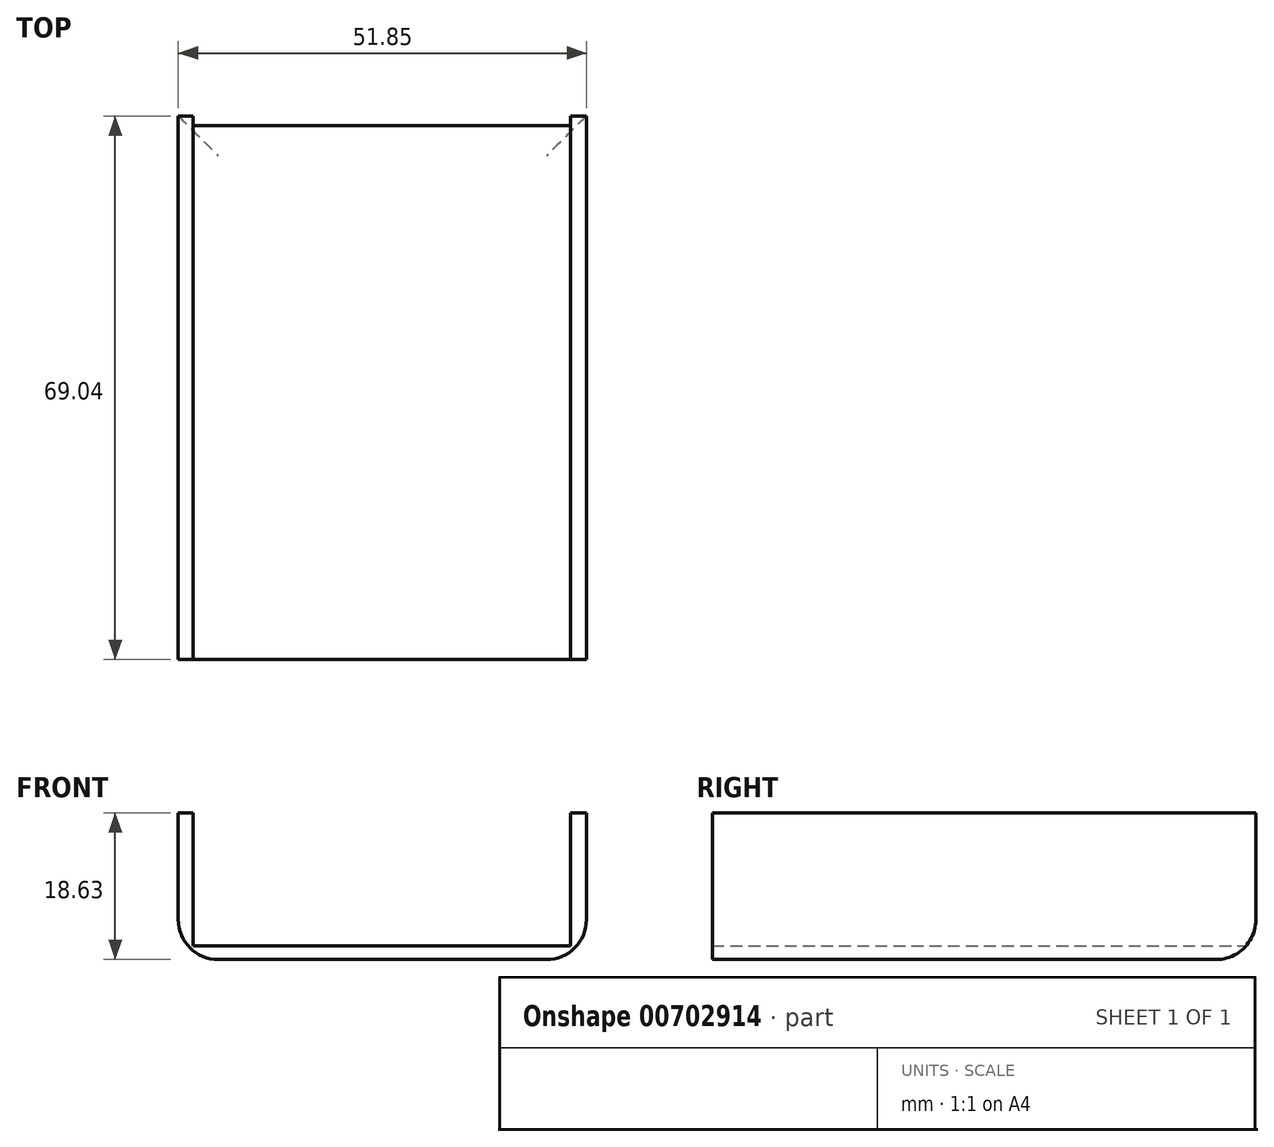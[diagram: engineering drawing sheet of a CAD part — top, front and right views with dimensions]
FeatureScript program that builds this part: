
annotation { "Feature Type Name" : "Feature", "Feature Type Description" : "" }
export const myFeature = defineFeature(function(context is Context, id is Id, definition is map)
    precondition{}
    {
        {
            var Q0;
            Q0=qCreatedBy(makeId("Front.planeOp"),FACE);
            var sketch = newSketch(context, id + "F0", { "sketchPlane" : qUnion([Q0])});
            skLineSegment(sketch, "E0.bottom", {"start": v(-24.96, -18.63) * mm, "end": v(26.89, -18.63) * mm});
            skLineSegment(sketch, "E0.left", {"start": v(-24.96, -18.63) * mm, "end": v(-24.96, 0) * mm});
            skLineSegment(sketch, "E0.right", {"start": v(26.89, -18.63) * mm, "end": v(26.89, 0) * mm});
            skPoint(sketch, "E0.middle", {"position": v(0, 0) * mm});
            skLineSegment(sketch, "E1", {"start": v(26.89, 0) * mm, "end": v(24.85, 0) * mm});
            skLineSegment(sketch, "E2.bottom", {"start": v(-23.06, -16.88) * mm, "end": v(24.85, -16.88) * mm});
            skLineSegment(sketch, "E2.left", {"start": v(-23.06, -16.88) * mm, "end": v(-23.06, 0) * mm});
            skLineSegment(sketch, "E2.right", {"start": v(24.85, -16.88) * mm, "end": v(24.85, 0) * mm});
            skLineSegment(sketch, "E3.trimOffspring", {"start": v(-23.06, 0) * mm, "end": v(-24.96, 0) * mm});
            skSolve(sketch);
        }
        {
            var Q0;
            Q0 = qSketchRegion(id + "F0", true);
            extrude(context, id + "F1", {"entities" : qUnion([Q0]), "endBound" : BoundingType.SYMMETRIC, "depth" : 69.05 * mm, "offsetDistance" : 25.4 * mm});
        }
        {
            var Q0;
            Q0=makeQuery(id+"F1.opExtrude","SWEPT_EDGE",EDGE,{"disambiguationData":[OSD([sQuery(id+"F0.wireOp",EDGE,"E0.bottom"),sQuery(id+"F0.wireOp",EDGE,"E0.right")])]});
            var Q1;
            Q1=makeQuery(id+"F1.opExtrude","SWEPT_EDGE",EDGE,{"disambiguationData":[OSD([sQuery(id+"F0.wireOp",EDGE,"E0.bottom"),sQuery(id+"F0.wireOp",EDGE,"E0.left")])]});
            var Q2;
            Q2=makeQuery(id+"F1.opExtrude","CAP_EDGE",EDGE,{"disambiguationData":[OSD([sQuery(id+"F0.wireOp",EDGE,"E0.bottom")])],"isStart":true});
            fillet(context, id + "F2", {"entities" : qUnion([Q0, Q1, Q2]), "radius" : 5.08 * mm, "tangentPropagation" : true, "allowEdgeOverflow" : false});
        }
    });
